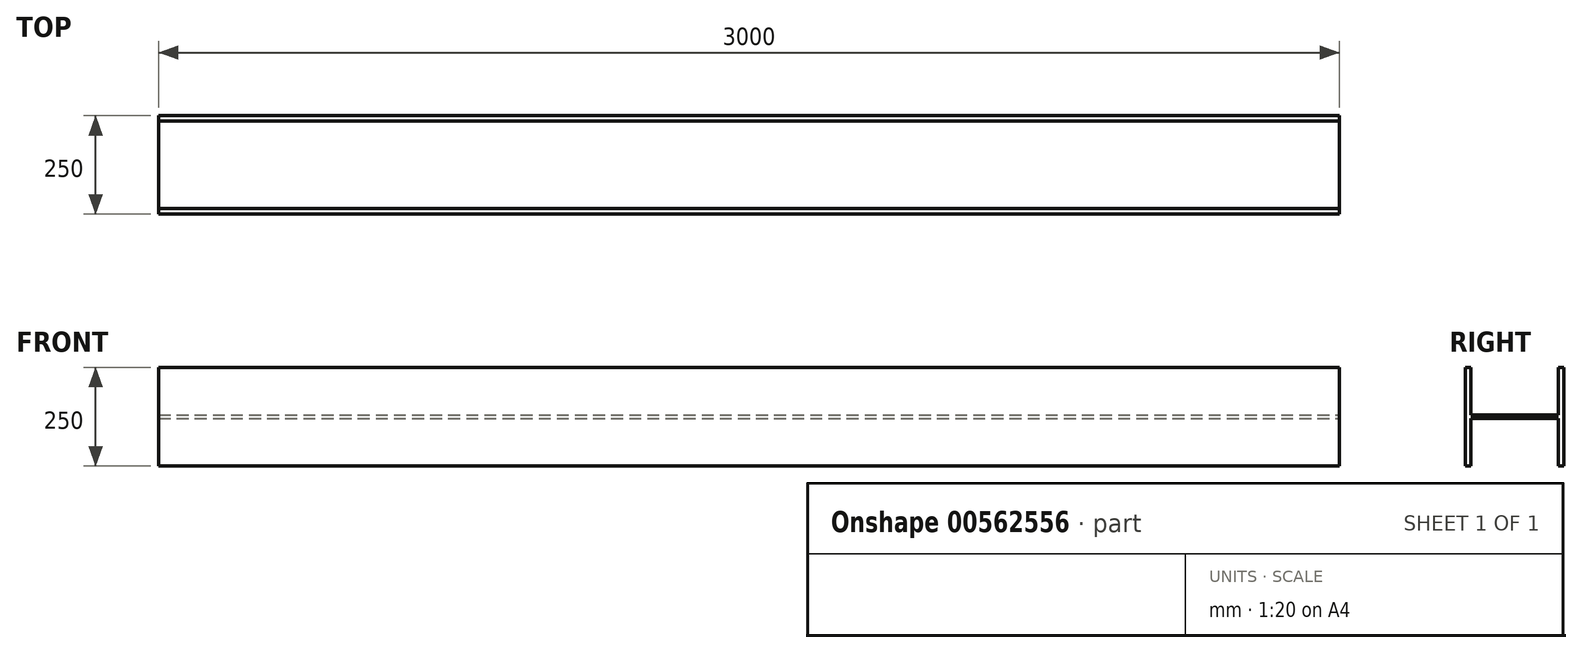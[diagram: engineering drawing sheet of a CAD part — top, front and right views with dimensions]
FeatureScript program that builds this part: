
annotation { "Feature Type Name" : "Feature", "Feature Type Description" : "" }
export const myFeature = defineFeature(function(context is Context, id is Id, definition is map)
    precondition{}
    {
        {
            var Q0;
            Q0=qCreatedBy(makeId("Top.planeOp"),FACE);
            var sketch = newSketch(context, id + "F0", { "sketchPlane" : qUnion([Q0])});
            skLineSegment(sketch, "E0", {"start": v(0, 250) * mm, "end": v(-125, 250) * mm});
            skLineSegment(sketch, "E1", {"start": v(-125, 250) * mm, "end": v(-125, 236) * mm});
            skLineSegment(sketch, "E2", {"start": v(-125, 236) * mm, "end": v(-4, 236) * mm});
            skLineSegment(sketch, "E3", {"start": v(-4, 236) * mm, "end": v(-4, 14) * mm});
            skLineSegment(sketch, "E4", {"start": v(-4, 14) * mm, "end": v(-125, 14) * mm});
            skLineSegment(sketch, "E5", {"start": v(-125, 14) * mm, "end": v(-125, 0) * mm});
            skLineSegment(sketch, "E6", {"start": v(-125, 0) * mm, "end": v(0, 0) * mm});
            skLineSegment(sketch, "E7.MirrorCS", {"start": v(125, 236) * mm, "end": v(4, 236) * mm});
            skLineSegment(sketch, "E8.MirrorCS", {"start": v(125, 0) * mm, "end": v(0, 0) * mm});
            skLineSegment(sketch, "E9.MirrorCS", {"start": v(125, 250) * mm, "end": v(125, 236) * mm});
            skLineSegment(sketch, "E10.MirrorCS", {"start": v(4, 14) * mm, "end": v(125, 14) * mm});
            skLineSegment(sketch, "E11.MirrorCS", {"start": v(0, 250) * mm, "end": v(125, 250) * mm});
            skLineSegment(sketch, "E12.MirrorCS", {"start": v(4, 236) * mm, "end": v(4, 14) * mm});
            skLineSegment(sketch, "E13.MirrorCS", {"start": v(125, 14) * mm, "end": v(125, 0) * mm});
            skSolve(sketch);
        }
        {
            var Q0;
            Q0=makeQuery(id+"F0.imprint","IMPRINT",FACE,{"disambiguationData":[TD([[makeQuery(id+"F0.imprint","IMPRINT",EDGE,{"derivedFrom":sQuery(id+"F0.wireOp",EDGE,"E0")}),1.0]])]});
            var Q1;
            Q1=makeQuery(id+"F0.imprint","IMPRINT",FACE,{"disambiguationData":[TD([[makeQuery(id+"F0.imprint","IMPRINT",EDGE,{"derivedFrom":sQuery(id+"F0.wireOp",EDGE,"E7.MirrorCS")}),-1.0]])]});
            extrude(context, id + "F1", {"entities" : qUnion([Q0, Q1]), "depth" : 3000 * mm, "offsetDistance" : 25 * mm});
        }
        {
            var Q0;
            Q0=makeQuery(id+"F1.opExtrude","SWEPT_BODY",BODY,{"disambiguationData":[OSD([sQuery(id+"F0.wireOp",EDGE,"E0"),sQuery(id+"F0.wireOp",EDGE,"E1"),sQuery(id+"F0.wireOp",EDGE,"E2"),sQuery(id+"F0.wireOp",EDGE,"E3"),sQuery(id+"F0.wireOp",EDGE,"E4"),sQuery(id+"F0.wireOp",EDGE,"E5"),sQuery(id+"F0.wireOp",EDGE,"E6"),sQuery(id+"F0.wireOp",EDGE,"E7.MirrorCS"),sQuery(id+"F0.wireOp",EDGE,"E8.MirrorCS"),sQuery(id+"F0.wireOp",EDGE,"E9.MirrorCS"),sQuery(id+"F0.wireOp",EDGE,"E10.MirrorCS"),sQuery(id+"F0.wireOp",EDGE,"E11.MirrorCS"),sQuery(id+"F0.wireOp",EDGE,"E12.MirrorCS"),sQuery(id+"F0.wireOp",EDGE,"E13.MirrorCS")])]});
            var Q1;
            Q1=makeQuery(id+"F1.opExtrude","CAP_EDGE",EDGE,{"disambiguationData":[OSD([sQuery(id+"F0.wireOp",EDGE,"E1")])],"isStart":true});
            transform(context, id + "F2", {"entities" : qUnion([Q0]), "transformType" : TransformType.ROTATION, "transformAxis" : qUnion([Q1]), "angle" : 90 * degree, "makeCopy" : false});
        }
    });
